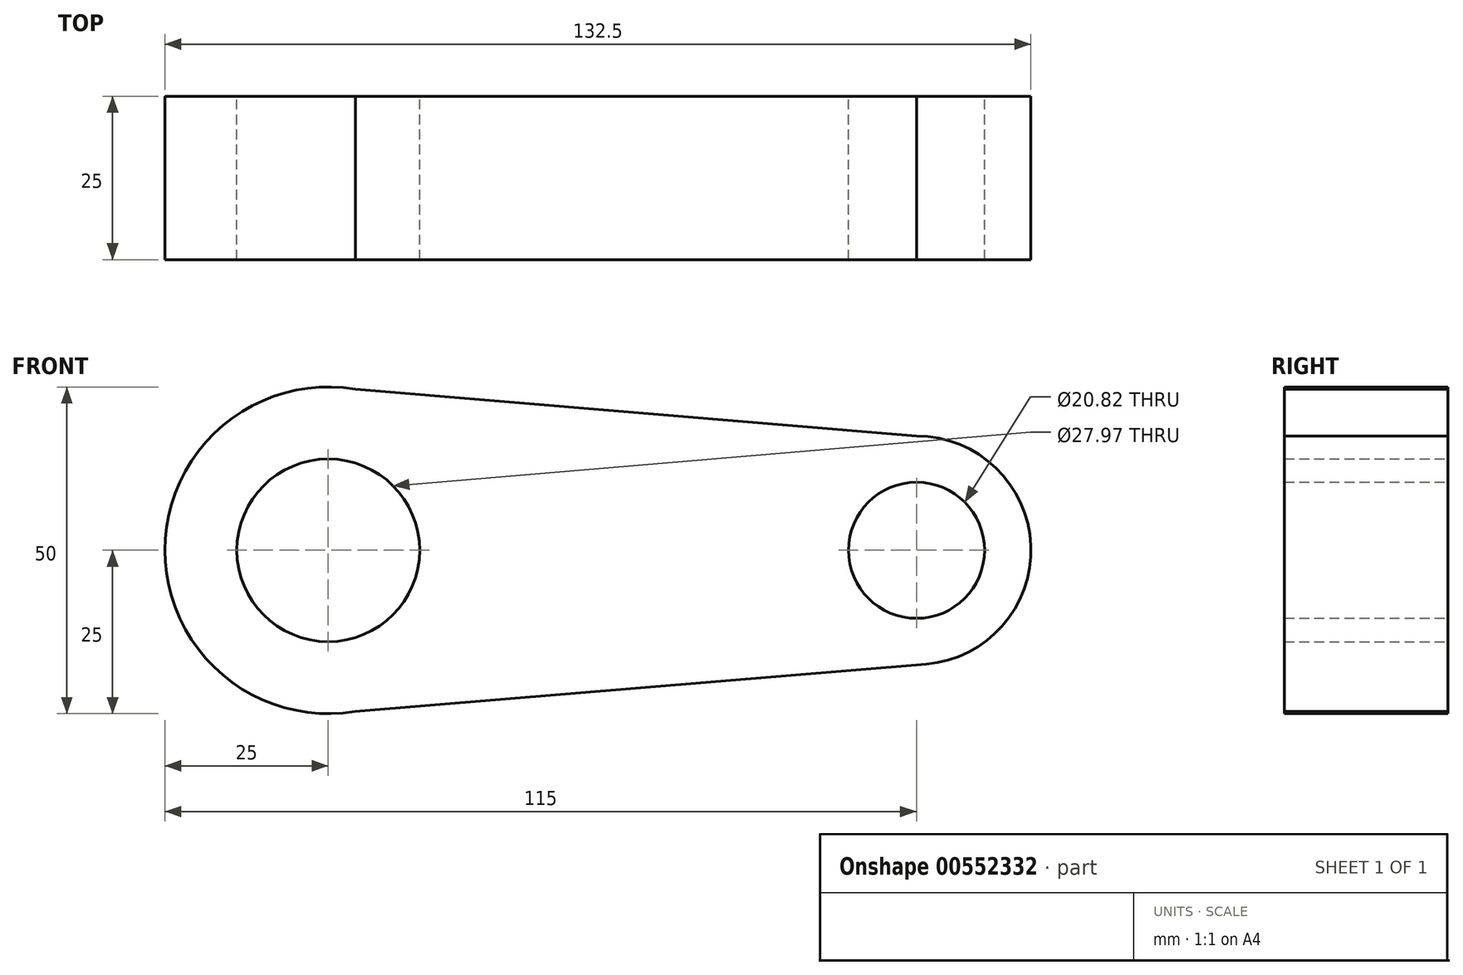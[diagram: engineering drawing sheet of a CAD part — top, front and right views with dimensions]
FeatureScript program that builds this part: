
annotation { "Feature Type Name" : "Feature", "Feature Type Description" : "" }
export const myFeature = defineFeature(function(context is Context, id is Id, definition is map)
    precondition{}
    {
        {
            var Q0;
            Q0=qCreatedBy(makeId("Front.planeOp"),FACE);
            var sketch = newSketch(context, id + "F0", { "sketchPlane" : qUnion([Q0])});
            skCircle(sketch, "E0", {"center": v(0, 0) * mm, "radius": 25 * mm});
            skCircle(sketch, "E1", {"center": v(90, 0) * mm, "radius": 17.5 * mm});
            skLineSegment(sketch, "E2", {"start": v(0, 25) * mm, "end": v(90, 17.5) * mm});
            skLineSegment(sketch, "E3", {"start": v(0, -25) * mm, "end": v(91.44, -17.44) * mm});
            skCircle(sketch, "E4", {"center": v(0, 0) * mm, "radius": 24.1 * mm});
            skCircle(sketch, "E5", {"center": v(0, 0) * mm, "radius": 13.98 * mm});
            skCircle(sketch, "E6", {"center": v(90, 0) * mm, "radius": 10.41 * mm});
            skSolve(sketch);
        }
        {
            var Q0;
            Q0 = qSketchRegion(id + "F0", true);
            var Q1;
            Q1=makeQuery(id+"F0.imprint","IMPRINT",FACE,{"disambiguationData":[TD([[makeQuery(id+"F0.imprint","IMPRINT",EDGE,{"derivedFrom":sQuery(id+"F0.wireOp",EDGE,"E4")}),1.0]])]});
            extrude(context, id + "F1", {"entities" : qUnion([Q0, Q1]), "depth" : 25 * mm, "offsetDistance" : 25 * mm});
        }
    });
